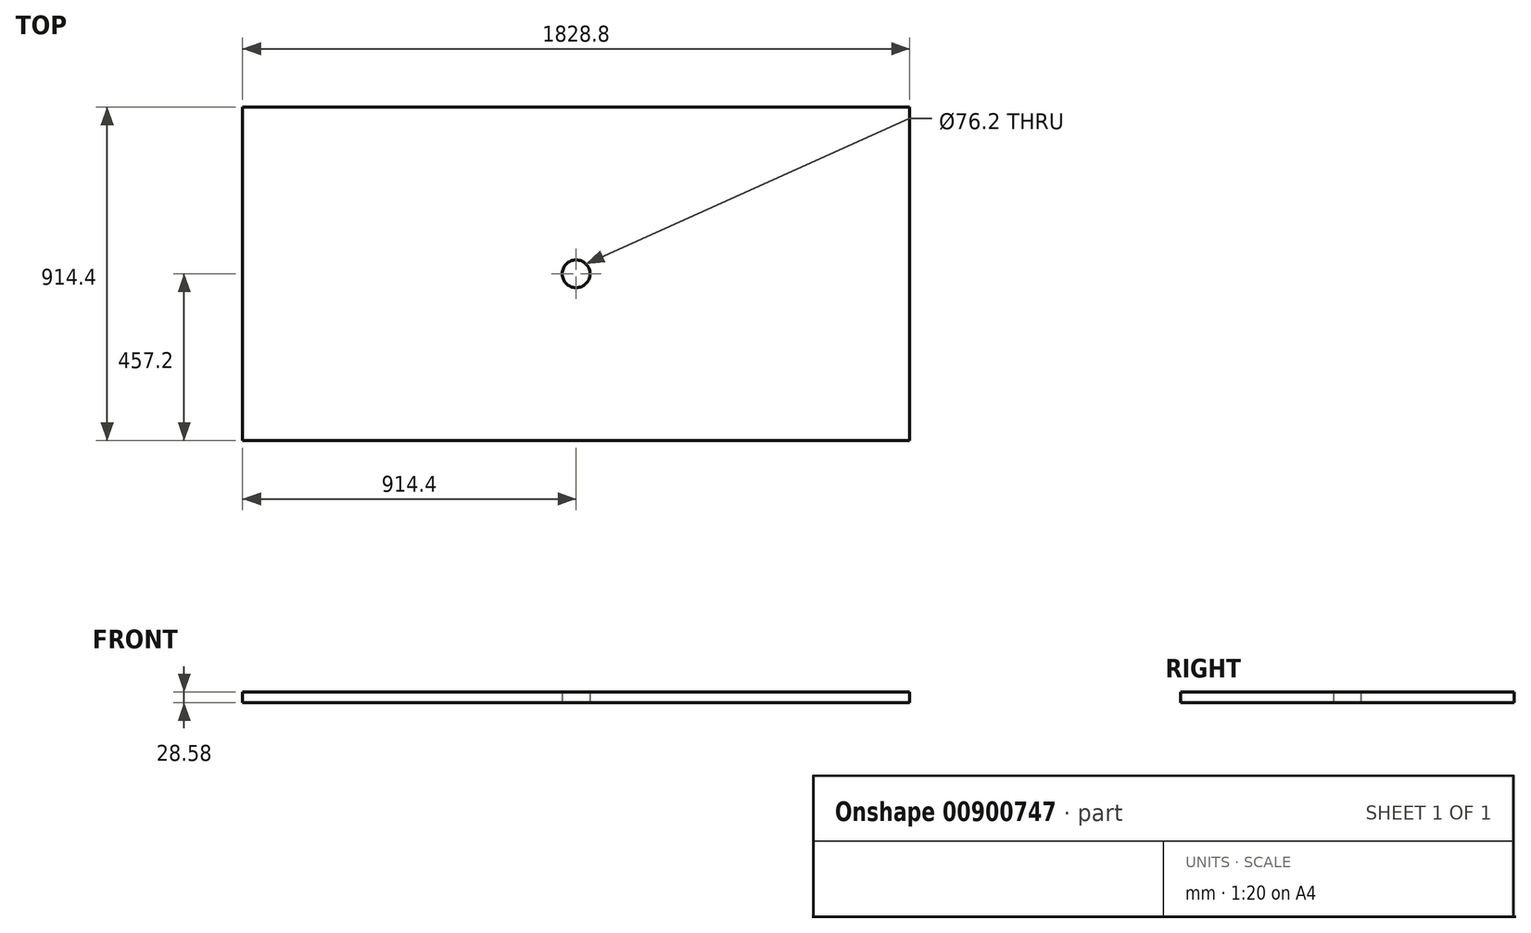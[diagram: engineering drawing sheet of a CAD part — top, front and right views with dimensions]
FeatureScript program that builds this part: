
annotation { "Feature Type Name" : "Feature", "Feature Type Description" : "" }
export const myFeature = defineFeature(function(context is Context, id is Id, definition is map)
    precondition{}
    {
        {
            var Q0;
            Q0=qCreatedBy(makeId("Top.planeOp"),FACE);
            var sketch = newSketch(context, id + "F0", { "sketchPlane" : qUnion([Q0])});
            skLineSegment(sketch, "E0.bottom", {"start": v(914.4, 457.2) * mm, "end": v(-914.4, 457.2) * mm});
            skLineSegment(sketch, "E0.top", {"start": v(914.4, -457.2) * mm, "end": v(-914.4, -457.2) * mm});
            skLineSegment(sketch, "E0.left", {"start": v(914.4, 457.2) * mm, "end": v(914.4, -457.2) * mm});
            skLineSegment(sketch, "E0.right", {"start": v(-914.4, 457.2) * mm, "end": v(-914.4, -457.2) * mm});
            skPoint(sketch, "E0.middle", {"position": v(0, 0) * mm});
            skCircle(sketch, "E1", {"center": v(0, 0) * mm, "radius": 38.1 * mm});
            skSolve(sketch);
        }
        {
            var Q0;
            Q0=makeQuery(id+"F0.imprint","IMPRINT",FACE,{"disambiguationData":[TD([[makeQuery(id+"F0.imprint","IMPRINT",EDGE,{"derivedFrom":sQuery(id+"F0.wireOp",EDGE,"E0.bottom")}),1.0]])]});
            extrude(context, id + "F1", {"entities" : qUnion([Q0]), "depth" : 28.57 * mm, "offsetDistance" : 25.4 * mm});
        }
    });
